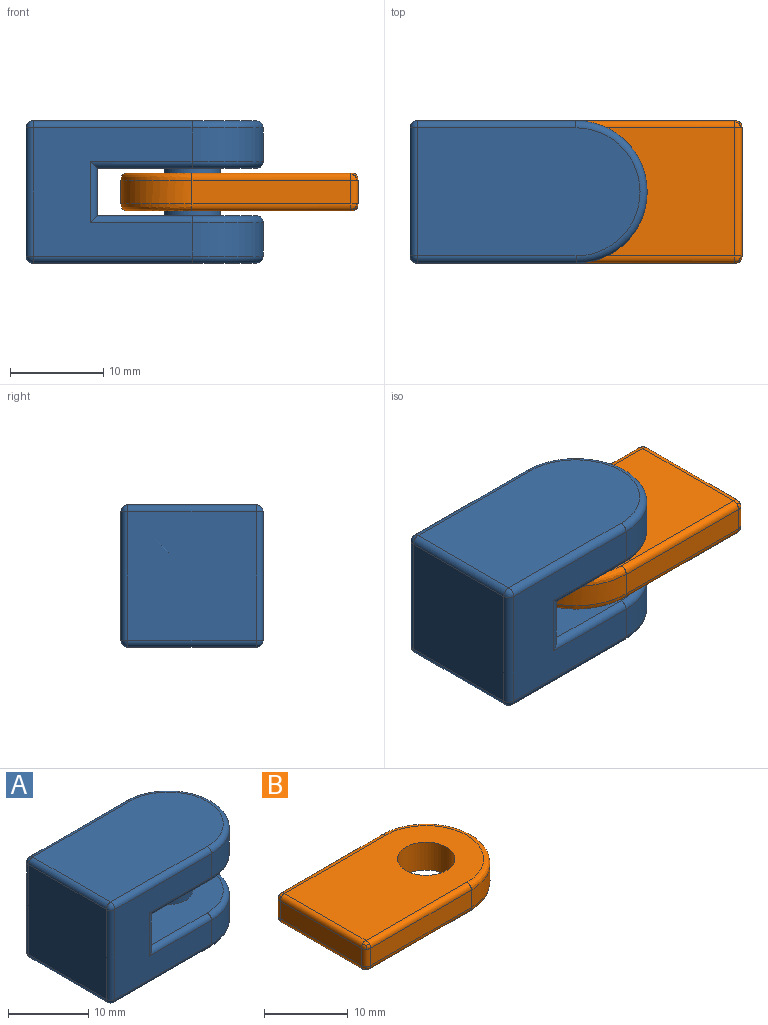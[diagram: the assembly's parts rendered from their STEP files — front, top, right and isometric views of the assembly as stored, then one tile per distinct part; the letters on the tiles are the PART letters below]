
ASSEMBLY  parts=2 mates=1
PART A: 33 faces, bbox 26x16.5x15.2 mm
  f0: plane 17.02x13.72mm, normal (0,0,1), area 184mm2, adj f7,f10,f11,f13,f15
  f1: plane 17.02x13.72mm, normal (0,0,-1), area 184mm2, adj f7,f10,f14,f16,f18
  f2: plane 17.02x13.72mm, normal (0,-1,0), area 161.3mm2, adj f3,f8,f15,f17,f18,f22,f28,f32
  f3: cylinder r=7.62mm len=15.24mm, axis (0,0,-1), area 85.1mm2, adj f2,f4,f13,f20
  f4: plane 17.02x13.72mm, normal (0,1,0), area 161.3mm2, adj f3,f8,f11,f12,f14,f19,f24,f27
  f5: plane 13.72x13.72mm, normal (-1,0,0), area 188.1mm2, adj f23,f24,f28,f29
  f6: plane 23.88x13.72mm, normal (0,0,-1), area 307.3mm2, adj f19,f20,f22,f23
  f7: cylinder r=3.05mm len=6.1mm, axis (0,0,-1), area 97.3mm2, adj f0,f1
  f8: cylinder r=7.62mm len=15.24mm, axis (0,0,-1), area 85.1mm2, adj f2,f4,f16,f30
  f9: plane 23.88x13.72mm, normal (0,0,1), area 307.3mm2, adj f27,f29,f30,f32
  f10: plane 13.72x5.08mm, normal (1,0,0), area 69.7mm2, adj f0,f1,f12,f17
  f11: cylinder r=0.76mm len=10.92mm, axis (1,0,0), area 12.5mm2, adj f0,f4,f12,f13
  f12: cylinder r=0.76mm len=6.6mm, axis (0,0,1), area 6.7mm2, adj f4,f10,f11,f14
  f13: torus R=6.86mm, axis (0,0,1), area 27.6mm2, adj f0,f3,f11,f15
  f14: cylinder r=0.76mm len=10.92mm, axis (-1,0,0), area 12.5mm2, adj f1,f4,f12,f16
  f15: cylinder r=0.76mm len=10.92mm, axis (-1,0,0), area 12.5mm2, adj f0,f2,f13,f17
  f16: torus R=6.86mm, axis (0,0,1), area 27.6mm2, adj f1,f8,f14,f18
  f17: cylinder r=0.76mm len=6.6mm, axis (0,0,-1), area 6.7mm2, adj f2,f10,f15,f18
  f18: cylinder r=0.76mm len=10.92mm, axis (1,0,0), area 12.5mm2, adj f1,f2,f16,f17
  f19: cylinder r=0.76mm len=17.02mm, axis (-1,0,0), area 20.4mm2, adj f4,f6,f20,f21
  f20: torus R=6.86mm, axis (0,0,1), area 27.6mm2, adj f3,f6,f19,f22
  f21: sphere r=0.76mm, area 0.9mm2, adj f19,f23,f24
  f22: cylinder r=0.76mm len=17.02mm, axis (1,0,0), area 20.4mm2, adj f2,f6,f20,f25
  f23: cylinder r=0.76mm len=13.72mm, axis (0,-1,0), area 16.4mm2, adj f5,f6,f21,f25
  f24: cylinder r=0.76mm len=13.72mm, axis (0,0,-1), area 16.4mm2, adj f4,f5,f21,f26
  f25: sphere r=0.76mm, area 0.9mm2, adj f22,f23,f28
  f26: sphere r=0.76mm, area 0.9mm2, adj f24,f27,f29
  f27: cylinder r=0.76mm len=17.02mm, axis (1,0,0), area 20.4mm2, adj f4,f9,f26,f30
  f28: cylinder r=0.76mm len=13.72mm, axis (0,0,1), area 16.4mm2, adj f2,f5,f25,f31
  f29: cylinder r=0.76mm len=13.72mm, axis (0,1,0), area 16.4mm2, adj f5,f9,f26,f31
  f30: torus R=6.86mm, axis (0,0,1), area 27.6mm2, adj f8,f9,f27,f32
  f31: sphere r=0.76mm, area 0.9mm2, adj f28,f29,f32
  f32: cylinder r=0.76mm len=17.02mm, axis (-1,0,0), area 20.4mm2, adj f2,f9,f30,f31
PART B: 29 faces, bbox 26.3x16.8x4.5 mm
  f0: plane 17.02x2.54mm, normal (0,-1,0), area 43.2mm2, adj f1,f15,f16,f17
  f1: cylinder r=7.62mm len=15.24mm, axis (0,0,-1), area 60.8mm2, adj f0,f2,f18,f21
  f2: plane 17.02x2.54mm, normal (0,1,0), area 43.2mm2, adj f1,f22,f25,f28
  f3: plane 13.72x2.54mm, normal (-1,0,0), area 34.8mm2, adj f16,f23,f24,f28
  f4: plane 23.9x13.74mm, normal (0,0,1), area 270.2mm2, adj f6,f15,f18,f22,f23
  f5: plane 23.9x13.74mm, normal (0,0,-1), area 270.2mm2, adj f6,f17,f21,f24,f25
  f6: cylinder r=3.43mm len=6.86mm, axis (0,0,1), area 87.6mm2, adj f4,f5
  f7: bspline ~0.59x0.59mm, area 0.4mm2, adj f8,f24,f25,f27
  f8: bspline ~0.59x0.59mm, area 0.4mm2, adj f7,f24,f27,f28
  f9: bspline ~0.59x0.59mm, area 0.4mm2, adj f10,f22,f23,f26
  f10: bspline ~0.59x0.59mm, area 0.4mm2, adj f9,f22,f26,f28
  f11: bspline ~0.59x0.59mm, area 0.4mm2, adj f12,f16,f17,f20
  f12: bspline ~0.59x0.59mm, area 0.4mm2, adj f11,f16,f20,f24
  f13: bspline ~0.59x0.59mm, area 0.4mm2, adj f14,f15,f16,f19
  f14: bspline ~0.59x0.59mm, area 0.4mm2, adj f13,f15,f19,f23
  f15: bspline ~18.67x0.76mm, area 21mm2, adj f0,f4,f13,f14,f18
  f16: bspline ~4.47x0.76mm, area 3.1mm2, adj f0,f3,f11,f12,f13,f19
  f17: bspline ~18.67x0.76mm, area 21mm2, adj f0,f5,f11,f20,f21
  f18: bspline ~15.24x7.62mm, area 28.6mm2, adj f1,f4,f15,f22
  f19: bspline ~0.59x0.59mm, area 0.4mm2, adj f13,f14,f16,f23
  f20: bspline ~0.59x0.59mm, area 0.4mm2, adj f11,f12,f17,f24
  f21: bspline ~15.24x7.62mm, area 28.6mm2, adj f1,f5,f17,f25
  f22: bspline ~18.67x0.76mm, area 21mm2, adj f2,f4,f9,f10,f18
  f23: bspline ~15.75x0.76mm, area 17mm2, adj f3,f4,f9,f14,f19,f26
  f24: bspline ~15.75x0.76mm, area 17mm2, adj f3,f5,f7,f8,f12,f20
  f25: bspline ~18.67x0.76mm, area 21mm2, adj f2,f5,f7,f21,f27
  f26: bspline ~0.59x0.59mm, area 0.4mm2, adj f9,f10,f23,f28
  f27: bspline ~0.59x0.59mm, area 0.4mm2, adj f7,f8,f25,f28
  f28: bspline ~4.47x0.76mm, area 3.1mm2, adj f2,f3,f8,f10,f26,f27
PLACE A t=(-14.3,-15.59,3.19)mm fixed
PLACE B rot(axis=(0,0,1),180deg) t=(-14.3,-15.59,8.77)mm
MATE revolute A.f3 <-> B.f1  axis (0,0,-1) through (-14.3,-15.59,8.27)mm
